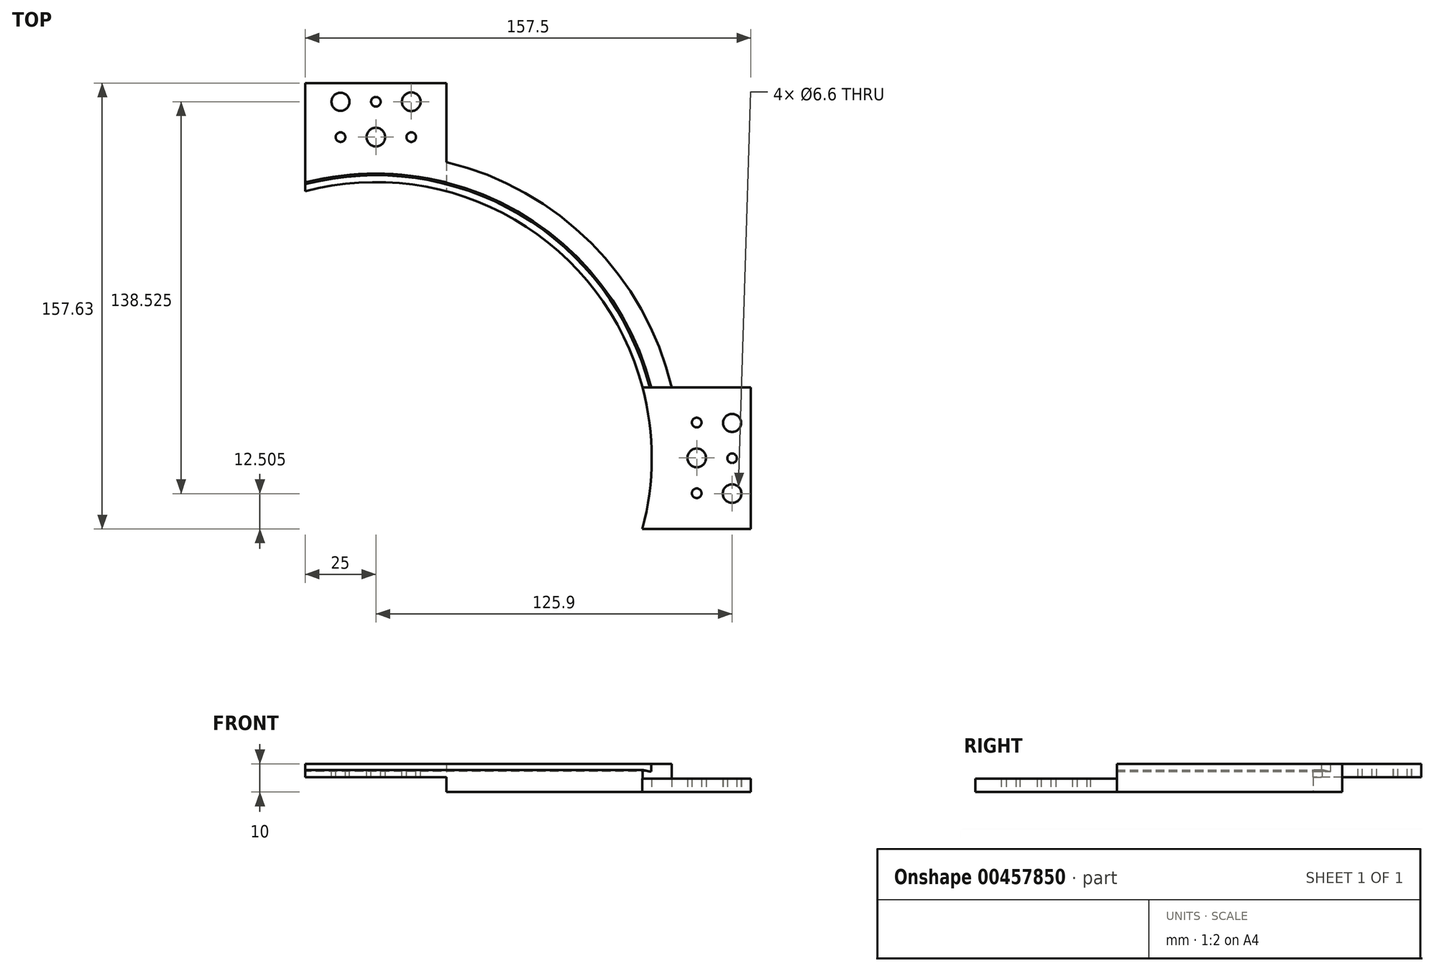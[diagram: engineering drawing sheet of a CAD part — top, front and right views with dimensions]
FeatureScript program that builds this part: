
annotation { "Feature Type Name" : "Feature", "Feature Type Description" : "" }
export const myFeature = defineFeature(function(context is Context, id is Id, definition is map)
    precondition{}
    {
        {
            var Q0;
            Q0=qCreatedBy(makeId("Top.planeOp"),FACE);
            var sketch = newSketch(context, id + "F0", { "sketchPlane" : qUnion([Q0])});
            skCircle(sketch, "E0", {"center": v(0, 0) * mm, "radius": 97.5 * mm});
            skCircle(sketch, "E1", {"center": v(0, 0) * mm, "radius": 107.5 * mm});
            skLineSegment(sketch, "E2", {"start": v(-97.5, 0) * mm, "end": v(-107.5, 0) * mm});
            skLineSegment(sketch, "E3", {"start": v(0, 97.5) * mm, "end": v(0, 107.5) * mm});
            skLineSegment(sketch, "E4", {"start": v(0, -97.5) * mm, "end": v(0, -107.5) * mm});
            skLineSegment(sketch, "E5.bottom", {"start": v(0, 97.5) * mm, "end": v(24.37, 97.5) * mm, "construction": true});
            skLineSegment(sketch, "E5.top", {"start": v(0, 132.5) * mm, "end": v(25, 132.5) * mm, "construction": true});
            skLineSegment(sketch, "E5.left", {"start": v(0, 97.5) * mm, "end": v(0, 132.5) * mm, "construction": true});
            skLineSegment(sketch, "E5.right", {"start": v(25, 97.5) * mm, "end": v(25, 132.5) * mm, "construction": true});
            skLineSegment(sketch, "E6.bottom", {"start": v(0, 132.5) * mm, "end": v(-25, 132.5) * mm, "construction": true});
            skLineSegment(sketch, "E6.top", {"start": v(0, 97.5) * mm, "end": v(-24.37, 97.5) * mm, "construction": true});
            skLineSegment(sketch, "E6.left", {"start": v(0, 132.5) * mm, "end": v(0, 97.5) * mm, "construction": true});
            skLineSegment(sketch, "E6.right", {"start": v(-25, 132.5) * mm, "end": v(-25, 97.5) * mm, "construction": true});
            skLineSegment(sketch, "E7.bottom", {"start": v(-25, 132.5) * mm, "end": v(25, 132.5) * mm});
            skLineSegment(sketch, "E7.top", {"start": v(-24.37, 97.5) * mm, "end": v(24.37, 97.5) * mm});
            skLineSegment(sketch, "E7.left", {"start": v(-25, 132.5) * mm, "end": v(-25, 97.5) * mm});
            skLineSegment(sketch, "E7.right", {"start": v(25, 132.5) * mm, "end": v(25, 97.5) * mm});
            skCircle(sketch, "E8", {"center": v(-12.5, 125.9) * mm, "radius": 3.2 * mm});
            skCircle(sketch, "E9", {"center": v(12.5, 125.9) * mm, "radius": 3.3 * mm});
            skLineSegment(sketch, "E10.top", {"start": v(97.48, -24.43) * mm, "end": v(97.48, -0.13) * mm, "construction": true});
            skLineSegment(sketch, "E11.left", {"start": v(97.48, 0.12) * mm, "end": v(97.48, 24.43) * mm, "construction": true});
            skLineSegment(sketch, "E12", {"start": v(0, 132.5) * mm, "end": v(0, 107.5) * mm});
            skLineSegment(sketch, "E13", {"start": v(-25, 97.5) * mm, "end": v(-25, 94.24) * mm});
            skLineSegment(sketch, "E14", {"start": v(25, 97.5) * mm, "end": v(25, 94.24) * mm});
            skArc(sketch, "E15", {"start": v(24.37, 97.5) * mm, "mid": v(0, 100.5) * mm, "end": v(-24.37, 97.5) * mm});
            skCircle(sketch, "E16", {"center": v(0, 113.4) * mm, "radius": 3.3 * mm});
            skCircle(sketch, "E17", {"center": v(12.5, 113.4) * mm, "radius": 1.7 * mm});
            skCircle(sketch, "E18", {"center": v(-12.5, 113.4) * mm, "radius": 1.7 * mm});
            skLineSegment(sketch, "E19", {"start": v(97.48, -0.13) * mm, "end": v(107.5, -0.13) * mm});
            skLineSegment(sketch, "E20.bottom", {"start": v(97.48, -0.13) * mm, "end": v(97.48, -24.43) * mm, "construction": true});
            skLineSegment(sketch, "E20.top", {"start": v(132.5, -0.13) * mm, "end": v(132.5, -25.13) * mm, "construction": true});
            skLineSegment(sketch, "E20.left", {"start": v(97.48, -0.13) * mm, "end": v(132.5, -0.13) * mm, "construction": true});
            skLineSegment(sketch, "E20.right", {"start": v(97.48, -25.13) * mm, "end": v(132.5, -25.13) * mm, "construction": true});
            skLineSegment(sketch, "E21.bottom", {"start": v(132.5, -0.13) * mm, "end": v(132.5, 24.87) * mm, "construction": true});
            skLineSegment(sketch, "E21.top", {"start": v(97.48, -0.13) * mm, "end": v(97.48, 24.43) * mm, "construction": true});
            skLineSegment(sketch, "E21.left", {"start": v(132.5, -0.13) * mm, "end": v(97.48, -0.13) * mm, "construction": true});
            skLineSegment(sketch, "E21.right", {"start": v(132.5, 24.87) * mm, "end": v(97.48, 24.87) * mm, "construction": true});
            skLineSegment(sketch, "E22.bottom", {"start": v(132.5, 24.87) * mm, "end": v(132.5, -25.13) * mm});
            skLineSegment(sketch, "E22.top", {"start": v(97.48, 24.43) * mm, "end": v(97.48, -24.43) * mm});
            skLineSegment(sketch, "E22.left", {"start": v(132.5, 24.87) * mm, "end": v(97.48, 24.87) * mm});
            skLineSegment(sketch, "E22.right", {"start": v(132.5, -25.13) * mm, "end": v(97.48, -25.13) * mm});
            skCircle(sketch, "E23", {"center": v(125.9, 12.37) * mm, "radius": 3.2 * mm});
            skCircle(sketch, "E24", {"center": v(125.9, -12.63) * mm, "radius": 3.3 * mm});
            skLineSegment(sketch, "E25", {"start": v(132.5, -0.13) * mm, "end": v(107.5, -0.13) * mm});
            skLineSegment(sketch, "E26", {"start": v(97.48, 24.87) * mm, "end": v(94.2, 24.87) * mm});
            skLineSegment(sketch, "E27", {"start": v(97.48, -25.13) * mm, "end": v(94.2, -25.13) * mm});
            skCircle(sketch, "E28", {"center": v(113.4, 0) * mm, "radius": 3.3 * mm});
            skCircle(sketch, "E29", {"center": v(113.4, -12.5) * mm, "radius": 1.7 * mm});
            skCircle(sketch, "E30", {"center": v(113.4, 12.5) * mm, "radius": 1.7 * mm});
            skArc(sketch, "E31.trimOffspring", {"start": v(-25, 97.34) * mm, "mid": v(-71.1, -71.02) * mm, "end": v(97.3, -25.13) * mm});
            skArc(sketch, "E32.trimOffspring", {"start": v(97.37, 24.87) * mm, "mid": v(71.1, 71.02) * mm, "end": v(25, 97.34) * mm});
            skArc(sketch, "E33.trimOffspring", {"start": v(97.48, -24.43) * mm, "mid": v(100.5, 0) * mm, "end": v(97.48, 24.43) * mm});
            skLineSegment(sketch, "E34", {"start": v(97.48, -24.43) * mm, "end": v(97.3, -25.13) * mm});
            skLineSegment(sketch, "E35", {"start": v(97.48, 24.43) * mm, "end": v(97.37, 24.87) * mm});
            skLineSegment(sketch, "E36", {"start": v(-25, 97.34) * mm, "end": v(-24.37, 97.5) * mm});
            skLineSegment(sketch, "E37", {"start": v(24.37, 97.5) * mm, "end": v(25, 97.34) * mm});
            skCircle(sketch, "E38", {"center": v(125.9, -0.13) * mm, "radius": 1.7 * mm});
            skCircle(sketch, "E39", {"center": v(0, 125.9) * mm, "radius": 1.7 * mm});
            skSolve(sketch);
        }
        {
            var Q0;
            {var subQ4=sQuery(id+"F0.wireOp",EDGE,"E14");Q0=makeQuery(id+"F0.imprint","IMPRINT",FACE,{"disambiguationData":[TD([[makeQuery(id+"F0.imprint","IMPRINT",EDGE,{"derivedFrom":subQ4}),1.0]])]});}
            var Q1;
            {var subQ7=sQuery(id+"F0.wireOp",EDGE,"E1");var subQ9=sQuery(id+"F0.wireOp",EDGE,"E22.left");var subQ10=makeQuery(id+"F0.imprint","INTERSECT",VERTEX,{"derivedFrom":[subQ7,subQ9]});Q1=makeQuery(id+"F0.imprint","IMPRINT",FACE,{"disambiguationData":[TD([[makeQuery(id+"F0.imprint","IMPRINT",EDGE,{"disambiguationData":[TD([[subQ10,-1.0]])],"derivedFrom":subQ7}),1.0]])]});}
            extrude(context, id + "F1", {"entities" : qUnion([Q0, Q1]), "depth" : 10 * mm});
        }
        {
            var Q0;
            Q0=makeQuery(id+"F1.opExtrude","CAP_FACE",FACE,{"disambiguationData":[OSD([sQuery(id+"F0.wireOp",EDGE,"E0"),sQuery(id+"F0.wireOp",EDGE,"E1"),sQuery(id+"F0.wireOp",EDGE,"E7.right"),sQuery(id+"F0.wireOp",EDGE,"E14"),sQuery(id+"F0.wireOp",EDGE,"E22.left"),sQuery(id+"F0.wireOp",EDGE,"E26")])],"isStart":false});
            var sketch = newSketch(context, id + "F2", { "sketchPlane" : qUnion([Q0])});
            skLineSegment(sketch, "E40.0.3", {"start": v(0, 100.5) * mm, "end": v(0, 100.5) * mm});
            skArc(sketch, "E41.0", {"start": v(24.37, 97.5) * mm, "mid": v(0, 100.5) * mm, "end": v(-24.37, 97.5) * mm});
            skLineSegment(sketch, "E42.0", {"start": v(0, 97.5) * mm, "end": v(0, 107.5) * mm});
            skLineSegment(sketch, "E43.0", {"start": v(-24.37, 97.5) * mm, "end": v(24.37, 97.5) * mm});
            skCircle(sketch, "E44.0", {"center": v(0, 0) * mm, "radius": 97.5 * mm});
            skLineSegment(sketch, "E45.0", {"start": v(24.37, 97.5) * mm, "end": v(25, 97.34) * mm});
            skLineSegment(sketch, "E46.0", {"start": v(25, 97.5) * mm, "end": v(25, 94.24) * mm});
            skLineSegment(sketch, "E47.0", {"start": v(25, 132.5) * mm, "end": v(25, 97.5) * mm});
            skLineSegment(sketch, "E48.0", {"start": v(-25, 97.5) * mm, "end": v(-25, 94.24) * mm});
            skLineSegment(sketch, "E49.0", {"start": v(-25, 97.34) * mm, "end": v(-24.37, 97.5) * mm});
            skLineSegment(sketch, "E50.0", {"start": v(-25, 132.5) * mm, "end": v(-25, 97.5) * mm});
            skCircle(sketch, "E51.0", {"center": v(0, 0) * mm, "radius": 107.5 * mm});
            skLineSegment(sketch, "E52.0", {"start": v(-25, 132.5) * mm, "end": v(25, 132.5) * mm});
            skCircle(sketch, "E53.0", {"center": v(12.5, 125.9) * mm, "radius": 3.3 * mm});
            skCircle(sketch, "E54.0.0", {"center": v(-12.5, 125.9) * mm, "radius": 3.2 * mm});
            skCircle(sketch, "E55.0", {"center": v(-12.5, 113.4) * mm, "radius": 1.7 * mm});
            skCircle(sketch, "E56.0", {"center": v(0, 113.4) * mm, "radius": 3.3 * mm});
            skCircle(sketch, "E57.0", {"center": v(12.5, 113.4) * mm, "radius": 1.7 * mm});
            skCircle(sketch, "E58.0", {"center": v(0, 125.9) * mm, "radius": 1.7 * mm});
            skSolve(sketch);
        }
        {
            var Q0;
            Q0=makeQuery(id+"F4.boolean.opBoolean","MERGE",FACE,{"derivedFrom":[makeQuery(id+"F1.opExtrude","CAP_FACE",FACE,{"disambiguationData":[OSD([sQuery(id+"F0.wireOp",EDGE,"E0"),sQuery(id+"F0.wireOp",EDGE,"E1"),sQuery(id+"F0.wireOp",EDGE,"E7.right"),sQuery(id+"F0.wireOp",EDGE,"E14"),sQuery(id+"F0.wireOp",EDGE,"E22.left"),sQuery(id+"F0.wireOp",EDGE,"E26")])],"isStart":false}),makeQuery(id+"F4.opExtrude","CAP_FACE",FACE,{"disambiguationData":[OSD([sQuery(id+"F2.wireOp",EDGE,"E44.0"),sQuery(id+"F2.wireOp",EDGE,"E46.0"),sQuery(id+"F2.wireOp",EDGE,"E47.0"),sQuery(id+"F2.wireOp",EDGE,"E48.0"),sQuery(id+"F2.wireOp",EDGE,"E50.0"),sQuery(id+"F2.wireOp",EDGE,"E52.0"),sQuery(id+"F2.wireOp",EDGE,"E53.0"),sQuery(id+"F2.wireOp",EDGE,"E54.0.0"),sQuery(id+"F2.wireOp",EDGE,"E55.0"),sQuery(id+"F2.wireOp",EDGE,"E56.0"),sQuery(id+"F2.wireOp",EDGE,"E57.0")])],"isStart":true})]});
            var sketch = newSketch(context, id + "F3", { "sketchPlane" : qUnion([Q0])});
            skCircle(sketch, "E59.0", {"center": v(0, 0) * mm, "radius": 97.5 * mm});
            skArc(sketch, "E60.0", {"start": v(-25, 97.34) * mm, "mid": v(-71.1, -71.02) * mm, "end": v(97.3, -25.13) * mm});
            skArc(sketch, "E61.0", {"start": v(24.37, 97.5) * mm, "mid": v(0, 100.5) * mm, "end": v(-24.37, 97.5) * mm});
            skArc(sketch, "E62.0", {"start": v(97.37, 24.87) * mm, "mid": v(71.1, 71.02) * mm, "end": v(25, 97.34) * mm});
            skLineSegment(sketch, "E63.0", {"start": v(-25, 97.34) * mm, "end": v(-24.37, 97.5) * mm});
            skPoint(sketch, "E64.0", {"position": v(24.69, 97.42) * mm});
            skLineSegment(sketch, "E65.0", {"start": v(24.37, 97.5) * mm, "end": v(25, 97.34) * mm});
            skLineSegment(sketch, "E66.0", {"start": v(97.48, 24.43) * mm, "end": v(97.37, 24.87) * mm});
            skArc(sketch, "E67.0", {"start": v(97.48, -24.43) * mm, "mid": v(100.5, 0) * mm, "end": v(97.48, 24.43) * mm});
            skLineSegment(sketch, "E68.0", {"start": v(97.48, -24.43) * mm, "end": v(97.3, -25.13) * mm});
            skSolve(sketch);
        }
        {
            var Q0;
            {var subQ6=sQuery(id+"F2.wireOp",EDGE,"E52.0");Q0=makeQuery(id+"F2.imprint","IMPRINT",FACE,{"disambiguationData":[TD([[makeQuery(id+"F2.imprint","IMPRINT",EDGE,{"derivedFrom":subQ6}),-1.0]])]});}
            var Q1;
            {var subQ0=sQuery(id+"F2.wireOp",EDGE,"E49.0");Q1=makeQuery(id+"F2.imprint","IMPRINT",FACE,{"disambiguationData":[TD([[makeQuery(id+"F2.imprint","IMPRINT",EDGE,{"derivedFrom":subQ0}),1.0]])]});}
            var Q2;
            {var subQ1=sQuery(id+"F2.wireOp",EDGE,"E45.0");Q2=makeQuery(id+"F2.imprint","IMPRINT",FACE,{"disambiguationData":[TD([[makeQuery(id+"F2.imprint","IMPRINT",EDGE,{"derivedFrom":subQ1}),1.0]])]});}
            var Q3;
            {var subQ1=sQuery(id+"F2.wireOp",EDGE,"E41.0");var subQ3=sQuery(id+"F2.wireOp",EDGE,"E42.0");var subQ4=makeQuery(id+"F2.imprint","INTERSECT",VERTEX,{"derivedFrom":[subQ1,subQ3]});Q3=makeQuery(id+"F2.imprint","IMPRINT",FACE,{"disambiguationData":[TD([[makeQuery(id+"F2.imprint","IMPRINT",EDGE,{"disambiguationData":[TD([[subQ4,1.0]])],"derivedFrom":subQ1}),1.0]])]});}
            var Q4;
            {var subQ1=sQuery(id+"F2.wireOp",EDGE,"E41.0");var subQ3=sQuery(id+"F2.wireOp",EDGE,"E42.0");var subQ4=makeQuery(id+"F2.imprint","INTERSECT",VERTEX,{"derivedFrom":[subQ1,subQ3]});Q4=makeQuery(id+"F2.imprint","IMPRINT",FACE,{"disambiguationData":[TD([[makeQuery(id+"F2.imprint","IMPRINT",EDGE,{"disambiguationData":[TD([[subQ4,-1.0]])],"derivedFrom":subQ1}),1.0]])]});}
            var Q5;
            {var subQ0=sQuery(id+"F2.wireOp",EDGE,"E49.0");Q5=makeQuery(id+"F2.imprint","IMPRINT",FACE,{"disambiguationData":[TD([[makeQuery(id+"F2.imprint","IMPRINT",EDGE,{"derivedFrom":subQ0}),-1.0]])]});}
            var Q6;
            {var subQ0=sQuery(id+"F2.wireOp",EDGE,"E45.0");Q6=makeQuery(id+"F2.imprint","IMPRINT",FACE,{"disambiguationData":[TD([[makeQuery(id+"F2.imprint","IMPRINT",EDGE,{"derivedFrom":subQ0}),-1.0]])]});}
            extrude(context, id + "F4", {"entities" : qUnion([Q0, Q1, Q2, Q3, Q4, Q5, Q6]), "operationType" : NewBodyOperationType.ADD, "oppositeDirection" : true, "depth" : 4.8 * mm});
        }
        {
            var Q0;
            {var subQ0=sQuery(id+"F0.wireOp",EDGE,"E26");var subQ4=sQuery(id+"F0.wireOp",EDGE,"E0");var subQ7=makeQuery(id+"F0.imprint","INTERSECT",VERTEX,{"derivedFrom":[subQ4,subQ0]});Q0=makeQuery(id+"F0.imprint","IMPRINT",FACE,{"disambiguationData":[TD([[makeQuery(id+"F0.imprint","IMPRINT",EDGE,{"disambiguationData":[TD([[subQ7,1.0]])],"derivedFrom":subQ0}),1.0]])]});}
            var Q1;
            {var subQ0=sQuery(id+"F0.wireOp",EDGE,"E22.top");var subQ3=sQuery(id+"F0.wireOp",EDGE,"E33.trimOffspring");var subQ5=makeQuery(id+"F0.imprint","INTERSECT",VERTEX,{"disambiguationData":[OD(1.0)],"derivedFrom":[subQ0,subQ3]});Q1=makeQuery(id+"F0.imprint","IMPRINT",FACE,{"disambiguationData":[TD([[makeQuery(id+"F0.imprint","IMPRINT",EDGE,{"disambiguationData":[TD([[subQ5,1.0]])],"derivedFrom":subQ3}),1.0]])]});}
            var Q2;
            {var subQ1=sQuery(id+"F0.wireOp",EDGE,"E22.top");var subQ5=sQuery(id+"F0.wireOp",EDGE,"E33.trimOffspring");var subQ6=makeQuery(id+"F0.imprint","INTERSECT",VERTEX,{"disambiguationData":[OD(1.0)],"derivedFrom":[subQ1,subQ5]});Q2=makeQuery(id+"F0.imprint","IMPRINT",FACE,{"disambiguationData":[TD([[makeQuery(id+"F0.imprint","IMPRINT",EDGE,{"disambiguationData":[TD([[subQ6,1.0]])],"derivedFrom":subQ5}),-1.0]])]});}
            var Q3;
            Q3=makeQuery(id+"F0.imprint","IMPRINT",FACE,{"disambiguationData":[TD([[makeQuery(id+"F0.imprint","IMPRINT",EDGE,{"derivedFrom":sQuery(id+"F0.wireOp",EDGE,"E23")}),-1.0]])]});
            var Q4;
            {var subQ0=sQuery(id+"F0.wireOp",EDGE,"E27");var subQ5=sQuery(id+"F0.wireOp",EDGE,"E0");var subQ7=makeQuery(id+"F0.imprint","INTERSECT",VERTEX,{"derivedFrom":[subQ5,subQ0]});Q4=makeQuery(id+"F0.imprint","IMPRINT",FACE,{"disambiguationData":[TD([[makeQuery(id+"F0.imprint","IMPRINT",EDGE,{"disambiguationData":[TD([[subQ7,1.0]])],"derivedFrom":subQ0}),-1.0]])]});}
            var Q5;
            {var subQ0=sQuery(id+"F0.wireOp",EDGE,"E22.top");var subQ3=sQuery(id+"F0.wireOp",EDGE,"E33.trimOffspring");var subQ5=makeQuery(id+"F0.imprint","INTERSECT",VERTEX,{"disambiguationData":[OD(0.0)],"derivedFrom":[subQ0,subQ3]});Q5=makeQuery(id+"F0.imprint","IMPRINT",FACE,{"disambiguationData":[TD([[makeQuery(id+"F0.imprint","IMPRINT",EDGE,{"disambiguationData":[TD([[subQ5,-1.0]])],"derivedFrom":subQ3}),1.0]])]});}
            var Q6;
            {var subQ1=sQuery(id+"F0.wireOp",EDGE,"E22.top");var subQ3=sQuery(id+"F0.wireOp",EDGE,"E33.trimOffspring");var subQ4=makeQuery(id+"F0.imprint","INTERSECT",VERTEX,{"disambiguationData":[OD(0.0)],"derivedFrom":[subQ1,subQ3]});Q6=makeQuery(id+"F0.imprint","IMPRINT",FACE,{"disambiguationData":[TD([[makeQuery(id+"F0.imprint","IMPRINT",EDGE,{"disambiguationData":[TD([[subQ4,-1.0]])],"derivedFrom":subQ3}),-1.0]])]});}
            var Q7;
            Q7=makeQuery(id+"F0.imprint","IMPRINT",FACE,{"disambiguationData":[TD([[makeQuery(id+"F0.imprint","IMPRINT",EDGE,{"derivedFrom":sQuery(id+"F0.wireOp",EDGE,"E24")}),-1.0]])]});
            extrude(context, id + "F5", {"entities" : qUnion([Q0, Q1, Q2, Q3, Q4, Q5, Q6, Q7]), "operationType" : NewBodyOperationType.ADD, "depth" : 4.8 * mm});
        }
        {
            var Q0;
            Q0=qCreatedBy(makeId("Right.planeOp"),FACE);
            var sketch = newSketch(context, id + "F6", { "sketchPlane" : qUnion([Q0])});
            skLineSegment(sketch, "E69", {"start": v(0, 0) * mm, "end": v(0, 32.62) * mm, "construction": true});
            skSolve(sketch);
        }
        {
            var Q0;
            {var subQ5=sQuery(id+"F3.wireOp",EDGE,"E62.0");Q0=makeQuery(id+"F3.imprint","IMPRINT",FACE,{"disambiguationData":[TD([[makeQuery(id+"F3.imprint","IMPRINT",EDGE,{"derivedFrom":subQ5}),1.0]])]});}
            var Q1;
            Q1=makeQuery(id+"F3.imprint","IMPRINT",FACE,{"disambiguationData":[TD([[makeQuery(id+"F3.imprint","IMPRINT",EDGE,{"derivedFrom":sQuery(id+"F3.wireOp",EDGE,"E60.0")}),1.0]])]});
            extrude(context, id + "F7", {"entities" : qUnion([Q0, Q1]), "operationType" : NewBodyOperationType.REMOVE, "oppositeDirection" : true, "depth" : 2.15 * mm});
        }
        {
            var Q0;
            Q0=makeQuery(id+"F4.opExtrude","SWEPT_FACE",FACE,{"disambiguationData":[OSD([sQuery(id+"F2.wireOp",EDGE,"E48.0"),sQuery(id+"F2.wireOp",EDGE,"E50.0")])]});
            var sketch = newSketch(context, id + "F8", { "sketchPlane" : qUnion([Q0])});
            skLineSegment(sketch, "E70", {"start": v(-94.24, 7.85) * mm, "end": v(-96.74, 7.25) * mm});
            skLineSegment(sketch, "E71", {"start": v(-96.74, 7.25) * mm, "end": v(-97.34, 7.25) * mm});
            skLineSegment(sketch, "E72", {"start": v(-97.34, 7.25) * mm, "end": v(-97.34, 7.85) * mm});
            skLineSegment(sketch, "E73", {"start": v(-97.34, 7.85) * mm, "end": v(-94.24, 7.85) * mm});
            skSolve(sketch);
        }
        {
            var Q0;
            Q0=makeQuery(id+"F8.imprint","IMPRINT",FACE,{"disambiguationData":[TD([[makeQuery(id+"F8.imprint","IMPRINT",EDGE,{"derivedFrom":sQuery(id+"F8.wireOp",EDGE,"E70")}),-1.0]])]});
            var Q1;
            Q1=sQuery(id+"F6.wireOp",EDGE,"E69");
            revolve(context, id + "F9", {"operationType" : NewBodyOperationType.REMOVE, "entities" : qUnion([Q0]), "axis" : qUnion([Q1]), "revolveType" : RevolveType.FULL, "oppositeDirection" : true});
        }
    });
